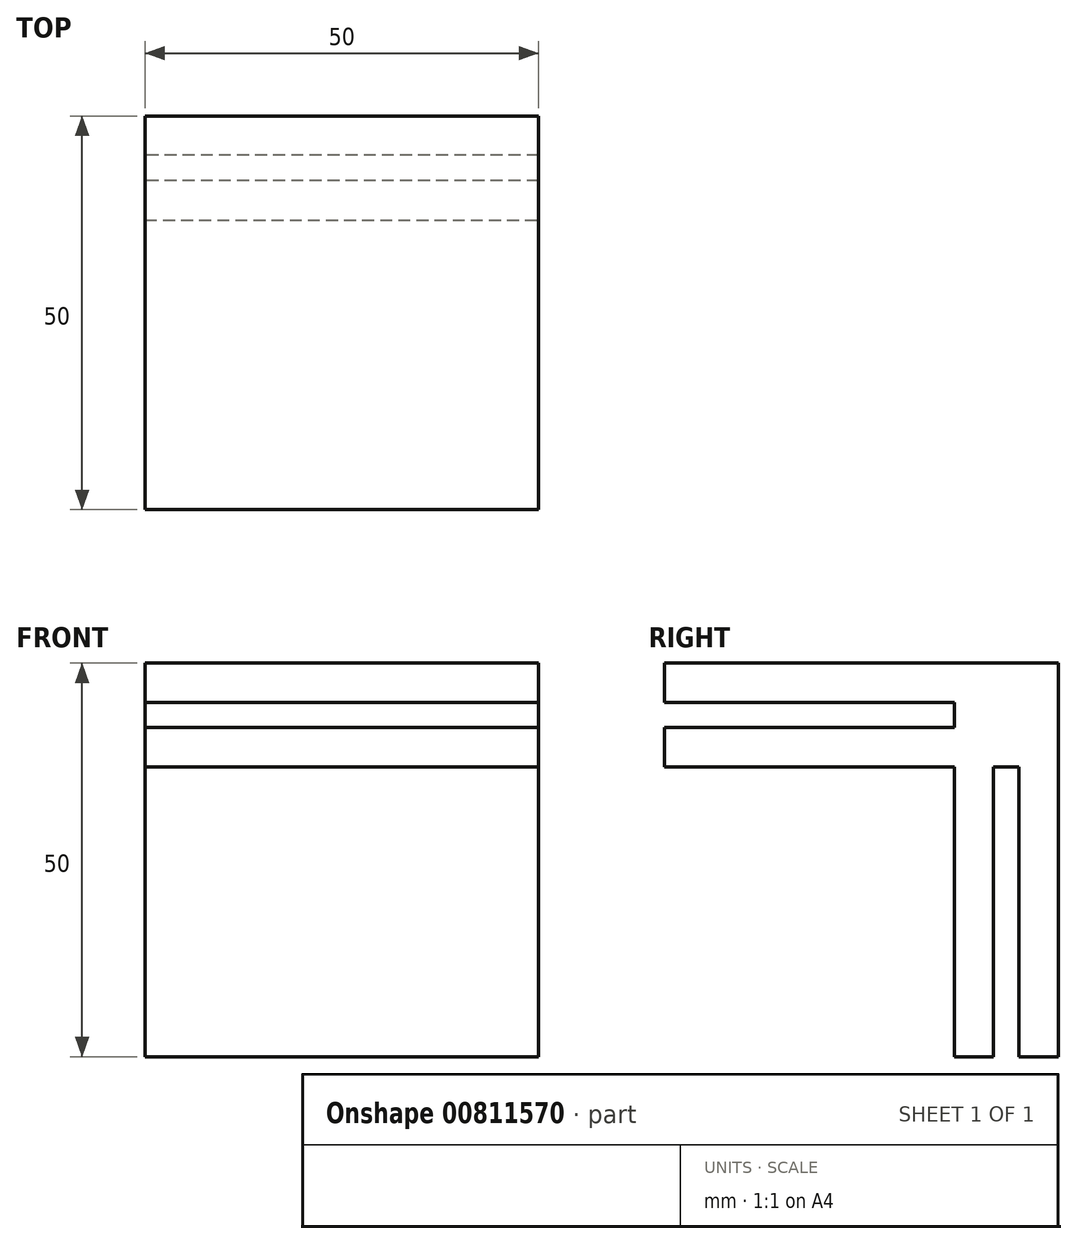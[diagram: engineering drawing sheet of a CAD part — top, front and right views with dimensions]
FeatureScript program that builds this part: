
annotation { "Feature Type Name" : "Feature", "Feature Type Description" : "" }
export const myFeature = defineFeature(function(context is Context, id is Id, definition is map)
    precondition{}
    {
        {
            var Q0;
            Q0=qCreatedBy(makeId("Top.planeOp"),FACE);
            var sketch = newSketch(context, id + "F0", { "sketchPlane" : qUnion([Q0])});
            skLineSegment(sketch, "E0.bottom", {"start": v(25, -25) * mm, "end": v(-25, -25) * mm});
            skLineSegment(sketch, "E0.top", {"start": v(25, 25) * mm, "end": v(-25, 25) * mm});
            skLineSegment(sketch, "E0.left", {"start": v(25, -25) * mm, "end": v(25, 25) * mm});
            skLineSegment(sketch, "E0.right", {"start": v(-25, -25) * mm, "end": v(-25, 25) * mm});
            skPoint(sketch, "E0.middle", {"position": v(0, 0) * mm});
            skSolve(sketch);
        }
        {
            var Q0;
            Q0=qSketchRegion(id+"F0",true);
            extrude(context, id + "F1", {"entities" : qUnion([Q0]), "depth" : 5 * mm, "offsetDistance" : 25 * mm});
        }
        {
            var Q0;
            Q0=makeQuery(id+"F1.opExtrude","SWEPT_FACE",FACE,{"disambiguationData":[OSD([sQuery(id+"F0.wireOp",EDGE,"E0.right")])]});
            var sketch = newSketch(context, id + "F2", { "sketchPlane" : qUnion([Q0])});
            skLineSegment(sketch, "E1.bottom", {"start": v(-25, 5) * mm, "end": v(-20, 5) * mm});
            skLineSegment(sketch, "E1.top", {"start": v(-25, -45) * mm, "end": v(-20, -45) * mm});
            skLineSegment(sketch, "E1.left", {"start": v(-25, 5) * mm, "end": v(-25, -45) * mm});
            skLineSegment(sketch, "E1.right", {"start": v(-20, 5) * mm, "end": v(-20, -45) * mm});
            skLineSegment(sketch, "E2.bottom", {"start": v(-16.8, 5) * mm, "end": v(-11.8, 5) * mm});
            skLineSegment(sketch, "E2.top", {"start": v(-16.8, -45) * mm, "end": v(-11.8, -45) * mm});
            skLineSegment(sketch, "E2.left", {"start": v(-16.8, 5) * mm, "end": v(-16.8, -45) * mm});
            skLineSegment(sketch, "E2.right", {"start": v(-11.8, 5) * mm, "end": v(-11.8, -45) * mm});
            skLineSegment(sketch, "E3", {"start": v(-22.5, -45) * mm, "end": v(-7.39, -45) * mm, "construction": true});
            skSolve(sketch);
        }
        {
            var Q0;
            Q0=qSketchRegion(id+"F2",true);
            var Q1;
            Q1 = qSketchRegion(id + "F8mCDAmMXpJjheD_3", true);
            var Q2;
            Q2=makeQuery(id+"F1.opExtrude","SWEPT_FACE",FACE,{"disambiguationData":[OSD([sQuery(id+"F0.wireOp",EDGE,"E0.left")])]});
            extrude(context, id + "F3", {"entities" : qUnion([Q0, Q1]), "operationType" : NewBodyOperationType.ADD, "endBound" : BoundingType.UP_TO_SURFACE, "oppositeDirection" : true, "depth" : 25 * mm, "endBoundEntityFace" : qUnion([Q2]), "offsetDistance" : 25 * mm});
        }
        {
            var Q0;
            Q0=makeQuery(id+"F3.opExtrude","SWEPT_FACE",FACE,{"disambiguationData":[OSD([sQuery(id+"F2.wireOp",EDGE,"E2.right")])]});
            var sketch = newSketch(context, id + "F4", { "sketchPlane" : qUnion([Q0])});
            skLineSegment(sketch, "E4.bottom", {"start": v(-25, -3.2) * mm, "end": v(25, -3.2) * mm});
            skLineSegment(sketch, "E4.top", {"start": v(-25, -8.2) * mm, "end": v(25, -8.2) * mm});
            skLineSegment(sketch, "E4.left", {"start": v(-25, -3.2) * mm, "end": v(-25, -8.2) * mm});
            skLineSegment(sketch, "E4.right", {"start": v(25, -3.2) * mm, "end": v(25, -8.2) * mm});
            skSolve(sketch);
        }
        {
            var Q0;
            Q0 = qSketchRegion(id + "F4", true);
            var Q1;
            Q1=makeQuery(id+"F1.opExtrude","SWEPT_FACE",FACE,{"disambiguationData":[OSD([sQuery(id+"F0.wireOp",EDGE,"E0.bottom")])]});
            extrude(context, id + "F5", {"entities" : qUnion([Q0]), "operationType" : NewBodyOperationType.ADD, "endBound" : BoundingType.UP_TO_SURFACE, "depth" : 25 * mm, "endBoundEntityFace" : qUnion([Q1]), "offsetDistance" : 25 * mm});
        }
        {
            var Q0;
            Q0=makeQuery(id+"F5.boolean.opBoolean","MERGE",FACE,{"derivedFrom":[makeQuery(id+"F3.boolean.opBoolean","MERGE",FACE,{"derivedFrom":[makeQuery(id+"F1.opExtrude","SWEPT_FACE",FACE,{"disambiguationData":[OSD([sQuery(id+"F0.wireOp",EDGE,"E0.right")])]}),makeQuery(id+"F3.opExtrude","CAP_FACE",FACE,{"disambiguationData":[OSD([sQuery(id+"F2.wireOp",EDGE,"E1.bottom"),sQuery(id+"F2.wireOp",EDGE,"E1.top"),sQuery(id+"F2.wireOp",EDGE,"E1.left"),sQuery(id+"F2.wireOp",EDGE,"E1.right")])],"isStart":true}),makeQuery(id+"F3.opExtrude","CAP_FACE",FACE,{"disambiguationData":[OSD([sQuery(id+"F2.wireOp",EDGE,"E2.bottom"),sQuery(id+"F2.wireOp",EDGE,"E2.top"),sQuery(id+"F2.wireOp",EDGE,"E2.left"),sQuery(id+"F2.wireOp",EDGE,"E2.right")])],"isStart":true})]}),makeQuery(id+"F5.opExtrude","SWEPT_FACE",FACE,{"disambiguationData":[OSD([sQuery(id+"F4.wireOp",EDGE,"E4.left")])]})]});
            var sketch = newSketch(context, id + "F6", { "sketchPlane" : qUnion([Q0])});
            skLineSegment(sketch, "E5.bottom", {"start": v(-16.8, -8.2) * mm, "end": v(-20, -8.2) * mm});
            skLineSegment(sketch, "E5.top", {"start": v(-16.8, 0) * mm, "end": v(-20, 0) * mm});
            skLineSegment(sketch, "E5.left", {"start": v(-16.8, -8.2) * mm, "end": v(-16.8, 0) * mm});
            skLineSegment(sketch, "E5.right", {"start": v(-20, -8.2) * mm, "end": v(-20, 0) * mm});
            skSolve(sketch);
        }
        {
            var Q0;
            Q0 = qSketchRegion(id + "F6", true);
            var Q1;
            Q1=makeQuery(id+"F5.boolean.opBoolean","MERGE",FACE,{"derivedFrom":[makeQuery(id+"F3.boolean.opBoolean","MERGE",FACE,{"derivedFrom":[makeQuery(id+"F1.opExtrude","SWEPT_FACE",FACE,{"disambiguationData":[OSD([sQuery(id+"F0.wireOp",EDGE,"E0.left")])]}),makeQuery(id+"F3.opExtrude","CAP_FACE",FACE,{"disambiguationData":[OSD([sQuery(id+"F2.wireOp",EDGE,"E1.bottom"),sQuery(id+"F2.wireOp",EDGE,"E1.top"),sQuery(id+"F2.wireOp",EDGE,"E1.left"),sQuery(id+"F2.wireOp",EDGE,"E1.right")])],"isStart":false}),makeQuery(id+"F3.opExtrude","CAP_FACE",FACE,{"disambiguationData":[OSD([sQuery(id+"F2.wireOp",EDGE,"E2.bottom"),sQuery(id+"F2.wireOp",EDGE,"E2.top"),sQuery(id+"F2.wireOp",EDGE,"E2.left"),sQuery(id+"F2.wireOp",EDGE,"E2.right")])],"isStart":false})]}),makeQuery(id+"F5.opExtrude","SWEPT_FACE",FACE,{"disambiguationData":[OSD([sQuery(id+"F4.wireOp",EDGE,"E4.right")])]})]});
            extrude(context, id + "F7", {"entities" : qUnion([Q0]), "operationType" : NewBodyOperationType.ADD, "endBound" : BoundingType.UP_TO_SURFACE, "oppositeDirection" : true, "depth" : 25 * mm, "endBoundEntityFace" : qUnion([Q1]), "offsetDistance" : 25 * mm});
        }
    });
